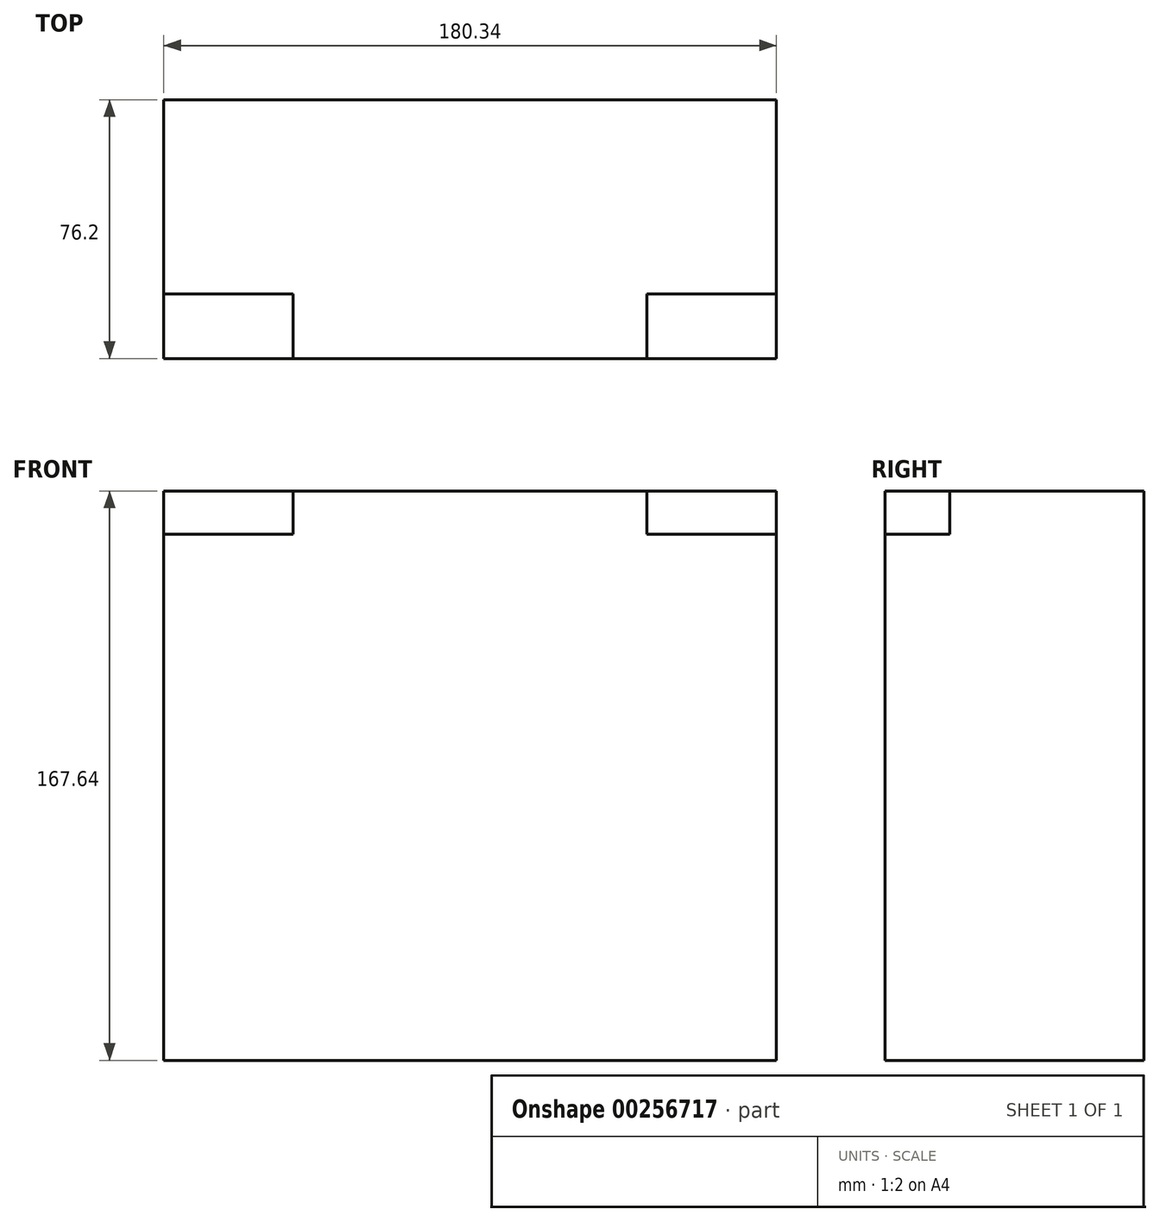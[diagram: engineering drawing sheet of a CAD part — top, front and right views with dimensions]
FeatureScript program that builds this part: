
annotation { "Feature Type Name" : "Feature", "Feature Type Description" : "" }
export const myFeature = defineFeature(function(context is Context, id is Id, definition is map)
    precondition{}
    {
        {
            var Q0;
            Q0=qCreatedBy(makeId("Top.planeOp"),FACE);
            var sketch = newSketch(context, id + "F0", { "sketchPlane" : qUnion([Q0])});
            skLineSegment(sketch, "E0", {"start": v(0, 0) * mm, "end": v(180.34, 0) * mm});
            skLineSegment(sketch, "E1", {"start": v(180.34, 0) * mm, "end": v(180.34, 76.2) * mm});
            skLineSegment(sketch, "E2", {"start": v(180.34, 76.2) * mm, "end": v(0, 76.2) * mm});
            skLineSegment(sketch, "E3", {"start": v(0, 76.2) * mm, "end": v(0, 0) * mm});
            skSolve(sketch);
        }
        {
            var Q0;
            Q0=makeQuery(id+"F0.imprint","IMPRINT",FACE,{"disambiguationData":[TD([[makeQuery(id+"F0.imprint","IMPRINT",EDGE,{"derivedFrom":sQuery(id+"F0.wireOp",EDGE,"E0")}),1.0]])]});
            extrude(context, id + "F1", {"entities" : qUnion([Q0]), "depth" : 167.64 * mm});
        }
        {
            var Q0;
            Q0=makeQuery(id+"F1.opExtrude","CAP_FACE",FACE,{"disambiguationData":[OSD([sQuery(id+"F0.wireOp",EDGE,"E0"),sQuery(id+"F0.wireOp",EDGE,"E1"),sQuery(id+"F0.wireOp",EDGE,"E2"),sQuery(id+"F0.wireOp",EDGE,"E3")])],"isStart":false});
            var sketch = newSketch(context, id + "F2", { "sketchPlane" : qUnion([Q0])});
            skLineSegment(sketch, "E4", {"start": v(0, 0) * mm, "end": v(0, 19.05) * mm});
            skLineSegment(sketch, "E5", {"start": v(0, 19.05) * mm, "end": v(38.1, 19.05) * mm});
            skLineSegment(sketch, "E6", {"start": v(38.1, 19.05) * mm, "end": v(38.1, 0) * mm});
            skLineSegment(sketch, "E7", {"start": v(38.1, 0) * mm, "end": v(0, 0) * mm});
            skLineSegment(sketch, "E8", {"start": v(180.34, 0) * mm, "end": v(180.34, 19.05) * mm});
            skLineSegment(sketch, "E9", {"start": v(180.34, 19.05) * mm, "end": v(142.24, 19.05) * mm});
            skLineSegment(sketch, "E10", {"start": v(142.24, 19.05) * mm, "end": v(142.24, 0) * mm});
            skLineSegment(sketch, "E11", {"start": v(142.24, 0) * mm, "end": v(180.34, 0) * mm});
            skSolve(sketch);
        }
        {
            var Q0;
            Q0=makeQuery(id+"F2.imprint","IMPRINT",FACE,{"disambiguationData":[TD([[makeQuery(id+"F2.imprint","IMPRINT",EDGE,{"derivedFrom":sQuery(id+"F2.wireOp",EDGE,"E4")}),1.0]])]});
            var Q1;
            Q1=makeQuery(id+"F2.imprint","IMPRINT",FACE,{"disambiguationData":[TD([[makeQuery(id+"F2.imprint","IMPRINT",EDGE,{"derivedFrom":sQuery(id+"F2.wireOp",EDGE,"E8")}),1.0]])]});
            extrude(context, id + "F3", {"entities" : qUnion([Q0, Q1]), "operationType" : NewBodyOperationType.REMOVE, "oppositeDirection" : true, "depth" : 12.7 * mm});
        }
    });
